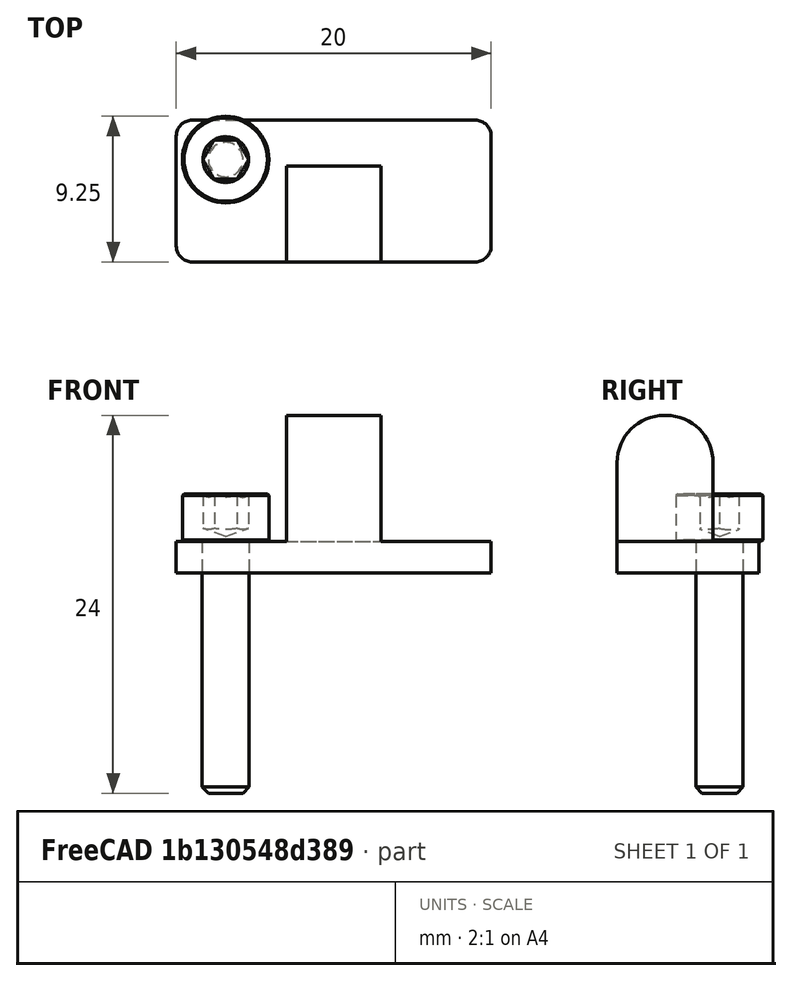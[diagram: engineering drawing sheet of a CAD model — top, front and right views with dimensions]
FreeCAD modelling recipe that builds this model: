
FCSTD DOCUMENT  (FreeCAD 0.16R6707 (Git))
Label: conector_fusor
License: All rights reserved
LicenseURL: http://en.wikipedia.org/wiki/All_rights_reserved
objects: Part::Box×2, Part::Fillet×2, Part::Feature×2, Mesh::Feature×1, Part::MultiFuse×1
note: 7 computed .brp shape members not serialized (recipe doc carries the construction recipe); baked Part::Feature solids carry a one-line shape summary decoded from their .brp

FEATURE [Mesh::Feature] gregs_wade_v5  label="gregs-wade-v5"
FEATURE [Part::Box] Box  label="Cubo"
  Height = 2
  Length = 20
  Width = 9
FEATURE [Part::Box] Box001  label="Cubo001"
  Height = 10
  Length = 6
  Placement = pos=(7,0,0) rot=(0,0,1;0rad)
  Width = 6.1
FEATURE [Part::Fillet] Fillet
  Base = -> Box001
  Edges = 2 edges r=3: [Edge10,Edge12]
FEATURE [Part::Fillet] Fillet001
  Base = -> Box
  Edges = 4 edges r=1: [Edge1,Edge3,Edge5,Edge7]
FEATURE [Part::MultiFuse] Fusion
  Placement = pos=(-2.7,-7,28) rot=(0,0,1;0rad)
  Shapes = -> [Fillet,Fillet001]
FEATURE [Part::Feature] Part__Feature  label="Chamfer001"
  Placement = pos=(0.44,-0.5,30) rot=(0,0,1;0rad)
  shape: bbox 5.5 x 5.5 x 19 mm, 16 faces (baked)
FEATURE [Part::Feature] Part__Feature001  label="Chamfer002"
  Placement = pos=(0.44,-0.5,30) rot=(0,0,1;0rad)
  shape: bbox 5.5 x 5.5 x 19 mm, 16 faces (baked)
